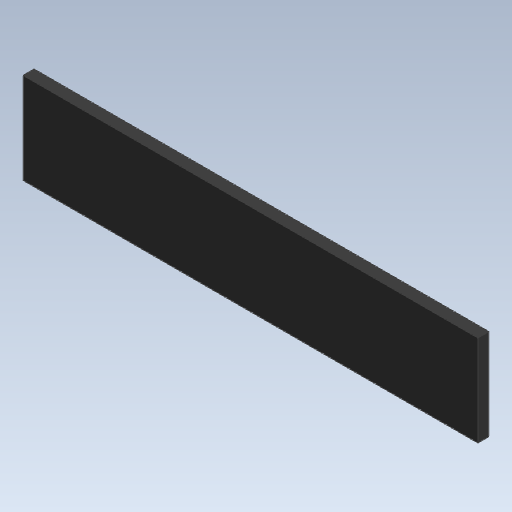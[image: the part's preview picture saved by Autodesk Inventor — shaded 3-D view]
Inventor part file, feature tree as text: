
AUTODESK INVENTOR PART (.ipt)
format: ipt  version: 2020 (Build 240168000, 168)  size: 93,184 bytes
history: native  units: mm
features: other x1, extrude x1
ambient origin geometry x8: Origin, YZ Plane, XZ Plane, XY Plane, X Axis, Y Axis, Z Axis, Center Point
bodies: Body1 (feature_tree)
feature tree (2):
  other  "實體1"
  extrude  "擠出1"  Depth=25.0mm
